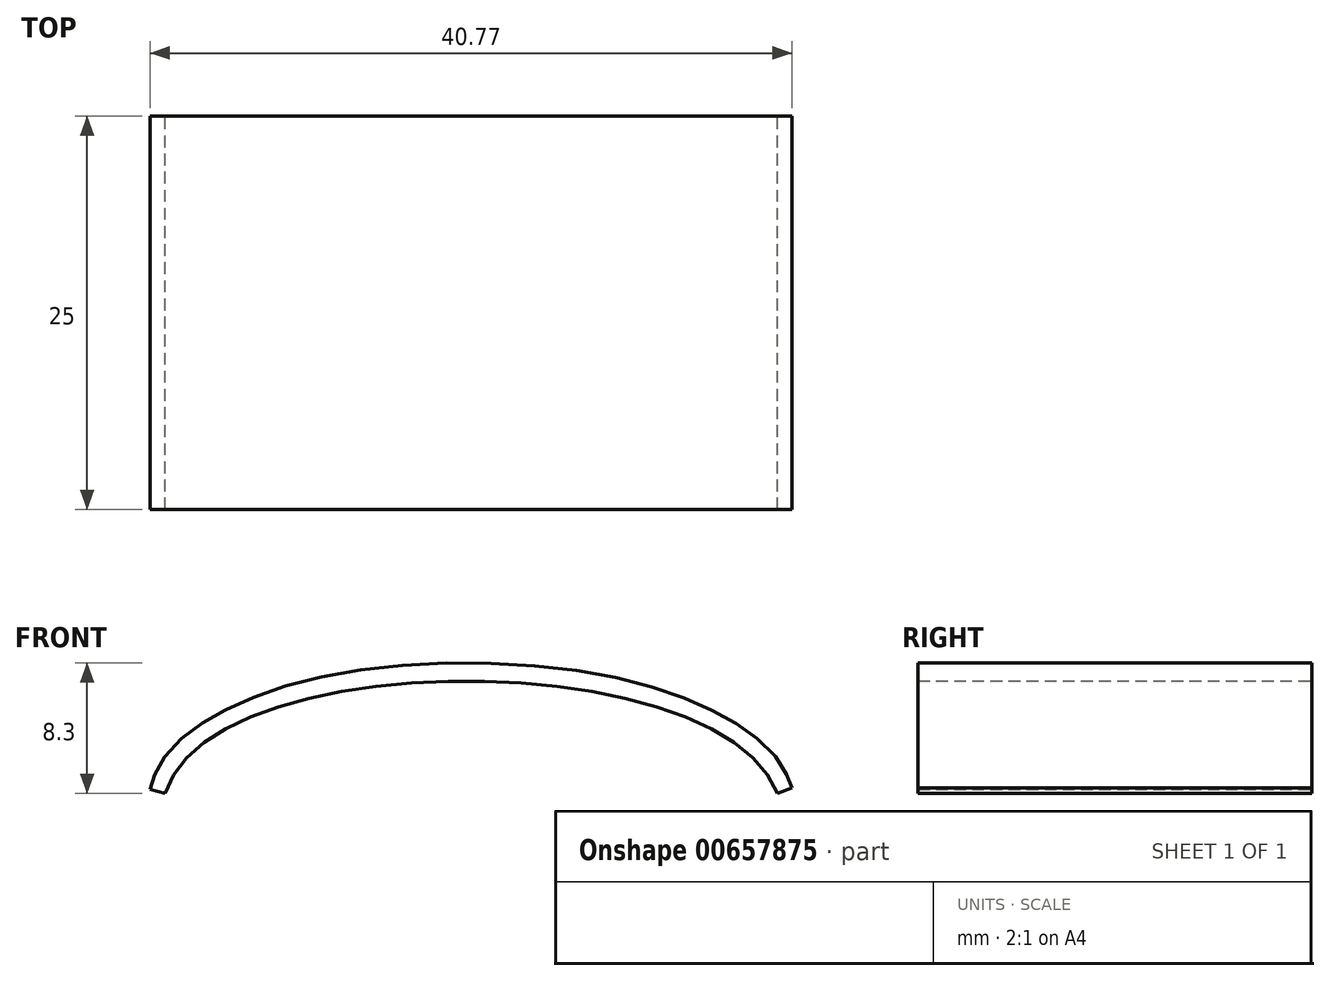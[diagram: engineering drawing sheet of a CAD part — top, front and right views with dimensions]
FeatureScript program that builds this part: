
annotation { "Feature Type Name" : "Feature", "Feature Type Description" : "" }
export const myFeature = defineFeature(function(context is Context, id is Id, definition is map)
    precondition{}
    {
        {
            var Q0;
            Q0=qCreatedBy(makeId("Front.planeOp"),FACE);
            var sketch = newSketch(context, id + "F0", { "sketchPlane" : qUnion([Q0])});
            skFitSpline(sketch, "E0", {"points": [v(-19.01, 0) * mm, v(19.87, 0) * mm], "startDerivative": vector(8.24, 28.6) * mm, "endDerivative": vector(10.82, -28.6) * mm});
            skFitSpline(sketch, "E1.0", {"points": [v(-19.97, 0.28) * mm, v(-19.76, 1) * mm, v(-19.07, 2.34) * mm, v(-17.4, 3.97) * mm, v(-15.23, 5.3) * mm, v(-11.8, 6.7) * mm, v(-6.7, 7.85) * mm, v(0.1, 8.3) * mm, v(6.95, 7.85) * mm, v(12.14, 6.7) * mm, v(15.68, 5.3) * mm, v(17.94, 3.99) * mm, v(19.73, 2.38) * mm, v(20.54, 1.07) * mm, v(20.8, 0.35) * mm]});
            skLineSegment(sketch, "E2", {"start": v(-19.97, 0.28) * mm, "end": v(-19.01, 0) * mm});
            skLineSegment(sketch, "E3", {"start": v(19.87, 0) * mm, "end": v(20.8, 0.35) * mm});
            skSolve(sketch);
        }
        {
            var Q0;
            Q0 = qSketchRegion(id + "F0", true);
            extrude(context, id + "F1", {"entities" : qUnion([Q0]), "depth" : 25 * mm, "offsetDistance" : 25 * mm});
        }
    });
